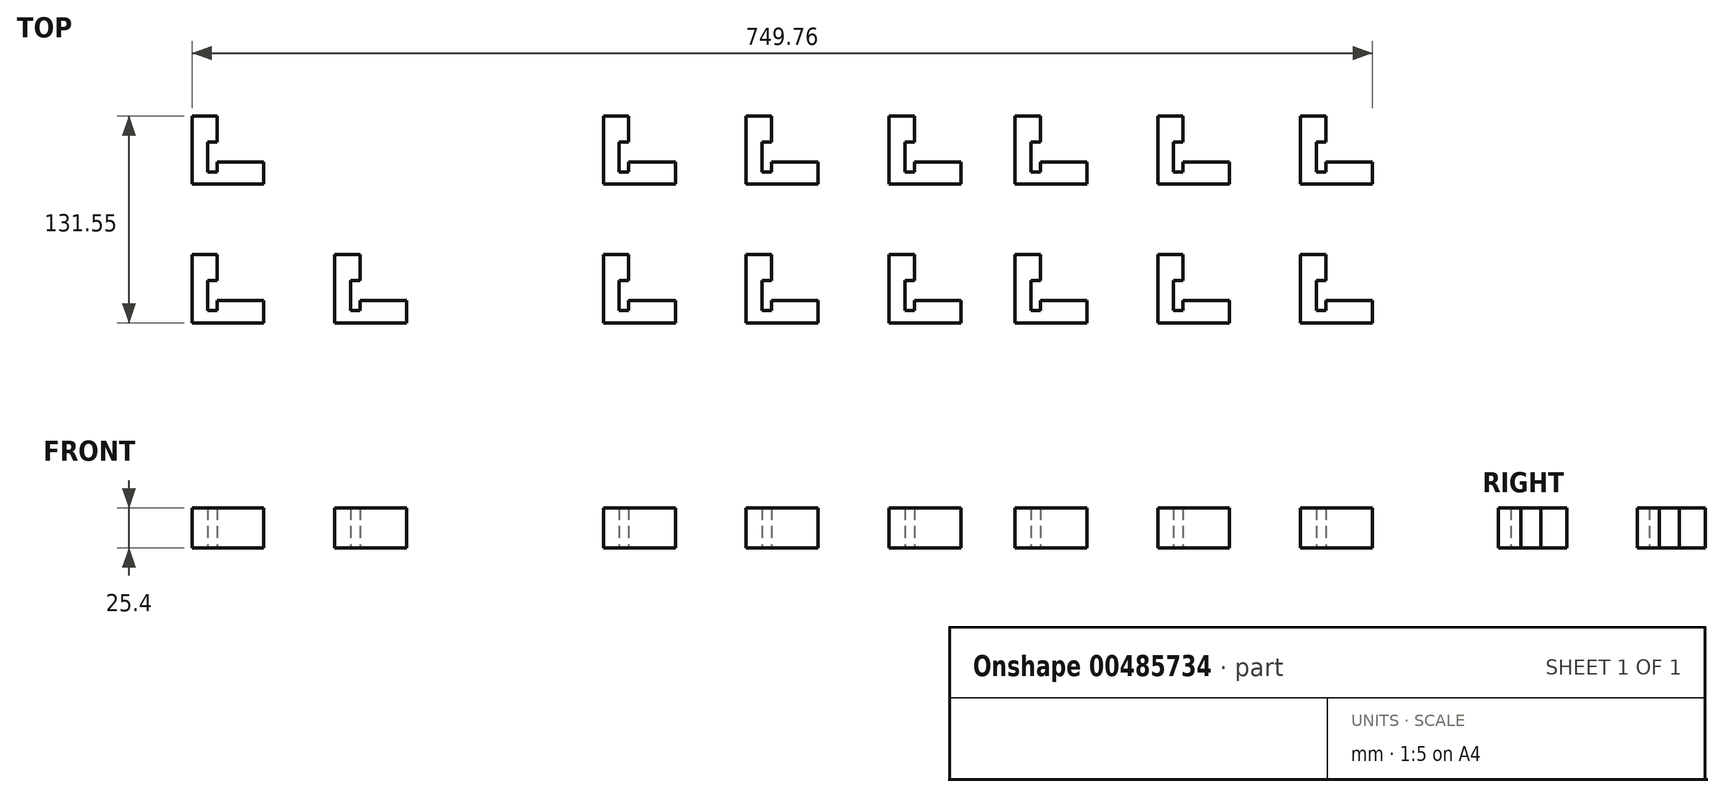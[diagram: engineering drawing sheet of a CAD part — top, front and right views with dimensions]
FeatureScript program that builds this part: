
annotation { "Feature Type Name" : "Feature", "Feature Type Description" : "" }
export const myFeature = defineFeature(function(context is Context, id is Id, definition is map)
    precondition{}
    {
        {
            var Q0;
            Q0=qCreatedBy(makeId("Top.planeOp"),FACE);
            var sketch = newSketch(context, id + "F0", { "sketchPlane" : qUnion([Q0])});
            skLineSegment(sketch, "E0.bottom", {"start": v(-6.8, 62.1) * mm, "end": v(-22.84, 62.1) * mm});
            skLineSegment(sketch, "E0.top", {"start": v(22.84, 18.7) * mm, "end": v(-22.84, 18.7) * mm});
            skLineSegment(sketch, "E0.left", {"start": v(22.84, 32.88) * mm, "end": v(22.84, 18.7) * mm});
            skLineSegment(sketch, "E0.right", {"start": v(-22.84, 62.1) * mm, "end": v(-22.84, 18.7) * mm});
            skLineSegment(sketch, "E1", {"start": v(-6.8, 62.1) * mm, "end": v(-6.8, 45.58) * mm});
            skLineSegment(sketch, "E2", {"start": v(-6.8, 45.58) * mm, "end": v(-12.8, 45.58) * mm});
            skLineSegment(sketch, "E3", {"start": v(-12.8, 45.58) * mm, "end": v(-12.8, 32.88) * mm});
            skLineSegment(sketch, "E4", {"start": v(-6.8, 32.88) * mm, "end": v(22.84, 32.88) * mm});
            skLineSegment(sketch, "E5", {"start": v(-6.8, 32.88) * mm, "end": v(-6.8, 26.57) * mm});
            skLineSegment(sketch, "E6", {"start": v(-6.8, 26.57) * mm, "end": v(-12.8, 26.57) * mm});
            skLineSegment(sketch, "E7", {"start": v(-12.8, 26.57) * mm, "end": v(-12.8, 32.88) * mm});
            skLineSegment(sketch, "E8.0.1.0", {"start": v(-6.8, 150.24) * mm, "end": v(-22.84, 150.24) * mm});
            skLineSegment(sketch, "E8.0.1.1", {"start": v(-6.8, 114.71) * mm, "end": v(-12.8, 114.71) * mm});
            skLineSegment(sketch, "E8.0.1.2", {"start": v(-12.8, 114.71) * mm, "end": v(-12.8, 121.02) * mm});
            skLineSegment(sketch, "E8.0.1.3", {"start": v(-6.8, 121.02) * mm, "end": v(22.84, 121.02) * mm});
            skLineSegment(sketch, "E8.0.1.4", {"start": v(-6.8, 150.24) * mm, "end": v(-6.8, 133.72) * mm});
            skLineSegment(sketch, "E8.0.1.5", {"start": v(-22.84, 150.24) * mm, "end": v(-22.84, 106.83) * mm});
            skLineSegment(sketch, "E8.0.1.6", {"start": v(-6.8, 133.72) * mm, "end": v(-12.8, 133.72) * mm});
            skLineSegment(sketch, "E8.0.1.7", {"start": v(-6.8, 121.02) * mm, "end": v(-6.8, 114.71) * mm});
            skLineSegment(sketch, "E8.0.1.8", {"start": v(-12.8, 133.72) * mm, "end": v(-12.8, 121.02) * mm});
            skLineSegment(sketch, "E8.0.1.9", {"start": v(22.84, 106.83) * mm, "end": v(-22.84, 106.83) * mm});
            skLineSegment(sketch, "E8.0.1.10", {"start": v(22.84, 121.02) * mm, "end": v(22.84, 106.83) * mm});
            skLineSegment(sketch, "E8.1.0.0", {"start": v(83.88, 62.1) * mm, "end": v(67.84, 62.1) * mm});
            skLineSegment(sketch, "E8.1.0.1", {"start": v(83.88, 26.57) * mm, "end": v(77.88, 26.57) * mm});
            skLineSegment(sketch, "E8.1.0.2", {"start": v(77.88, 26.57) * mm, "end": v(77.88, 32.88) * mm});
            skLineSegment(sketch, "E8.1.0.3", {"start": v(83.88, 32.88) * mm, "end": v(113.51, 32.88) * mm});
            skLineSegment(sketch, "E8.1.0.4", {"start": v(83.88, 62.1) * mm, "end": v(83.88, 45.58) * mm});
            skLineSegment(sketch, "E8.1.0.5", {"start": v(67.84, 62.1) * mm, "end": v(67.84, 18.7) * mm});
            skLineSegment(sketch, "E8.1.0.6", {"start": v(83.88, 45.58) * mm, "end": v(77.88, 45.58) * mm});
            skLineSegment(sketch, "E8.1.0.7", {"start": v(83.88, 32.88) * mm, "end": v(83.88, 26.57) * mm});
            skLineSegment(sketch, "E8.1.0.8", {"start": v(77.88, 45.58) * mm, "end": v(77.88, 32.88) * mm});
            skLineSegment(sketch, "E8.1.0.9", {"start": v(113.51, 18.7) * mm, "end": v(67.84, 18.7) * mm});
            skLineSegment(sketch, "E8.1.0.10", {"start": v(113.51, 32.88) * mm, "end": v(113.51, 18.7) * mm});
            skLineSegment(sketch, "E8.1.1.0", {"start": v(83.88, 150.24) * mm, "end": v(67.84, 150.24) * mm});
            skLineSegment(sketch, "E8.1.1.1", {"start": v(83.88, 114.71) * mm, "end": v(77.88, 114.71) * mm});
            skLineSegment(sketch, "E8.1.1.2", {"start": v(77.88, 114.71) * mm, "end": v(77.88, 121.02) * mm});
            skLineSegment(sketch, "E8.1.1.3", {"start": v(83.88, 121.02) * mm, "end": v(113.51, 121.02) * mm});
            skLineSegment(sketch, "E8.1.1.4", {"start": v(83.88, 150.24) * mm, "end": v(83.88, 133.72) * mm});
            skLineSegment(sketch, "E8.1.1.5", {"start": v(67.84, 150.24) * mm, "end": v(67.84, 106.83) * mm});
            skLineSegment(sketch, "E8.1.1.6", {"start": v(83.88, 133.72) * mm, "end": v(77.88, 133.72) * mm});
            skLineSegment(sketch, "E8.1.1.7", {"start": v(83.88, 121.02) * mm, "end": v(83.88, 114.71) * mm});
            skLineSegment(sketch, "E8.1.1.8", {"start": v(77.88, 133.72) * mm, "end": v(77.88, 121.02) * mm});
            skLineSegment(sketch, "E8.1.1.9", {"start": v(113.51, 106.83) * mm, "end": v(67.84, 106.83) * mm});
            skLineSegment(sketch, "E8.1.1.10", {"start": v(113.51, 121.02) * mm, "end": v(113.51, 106.83) * mm});
            skLineSegment(sketch, "E8.2.0.0", {"start": v(174.55, 62.1) * mm, "end": v(158.52, 62.1) * mm});
            skLineSegment(sketch, "E8.2.0.1", {"start": v(174.55, 26.57) * mm, "end": v(168.56, 26.57) * mm});
            skLineSegment(sketch, "E8.2.0.2", {"start": v(168.56, 26.57) * mm, "end": v(168.56, 32.88) * mm});
            skLineSegment(sketch, "E8.2.0.3", {"start": v(174.55, 32.88) * mm, "end": v(204.2, 32.88) * mm});
            skLineSegment(sketch, "E8.2.0.4", {"start": v(174.55, 62.1) * mm, "end": v(174.55, 45.58) * mm});
            skLineSegment(sketch, "E8.2.0.5", {"start": v(158.52, 62.1) * mm, "end": v(158.52, 18.7) * mm});
            skLineSegment(sketch, "E8.2.0.6", {"start": v(174.55, 45.58) * mm, "end": v(168.56, 45.58) * mm});
            skLineSegment(sketch, "E8.2.0.7", {"start": v(174.55, 32.88) * mm, "end": v(174.55, 26.57) * mm});
            skLineSegment(sketch, "E8.2.0.8", {"start": v(168.56, 45.58) * mm, "end": v(168.56, 32.88) * mm});
            skLineSegment(sketch, "E8.2.0.9", {"start": v(204.2, 18.7) * mm, "end": v(158.52, 18.7) * mm});
            skLineSegment(sketch, "E8.2.0.10", {"start": v(204.2, 32.88) * mm, "end": v(204.2, 18.7) * mm});
            skLineSegment(sketch, "E8.2.1.0", {"start": v(174.55, 150.24) * mm, "end": v(158.52, 150.24) * mm});
            skLineSegment(sketch, "E8.2.1.1", {"start": v(174.55, 114.71) * mm, "end": v(168.56, 114.71) * mm});
            skLineSegment(sketch, "E8.2.1.2", {"start": v(168.56, 114.71) * mm, "end": v(168.56, 121.02) * mm});
            skLineSegment(sketch, "E8.2.1.3", {"start": v(174.55, 121.02) * mm, "end": v(204.2, 121.02) * mm});
            skLineSegment(sketch, "E8.2.1.4", {"start": v(174.55, 150.24) * mm, "end": v(174.55, 133.72) * mm});
            skLineSegment(sketch, "E8.2.1.5", {"start": v(158.52, 150.24) * mm, "end": v(158.52, 106.83) * mm});
            skLineSegment(sketch, "E8.2.1.6", {"start": v(174.55, 133.72) * mm, "end": v(168.56, 133.72) * mm});
            skLineSegment(sketch, "E8.2.1.7", {"start": v(174.55, 121.02) * mm, "end": v(174.55, 114.71) * mm});
            skLineSegment(sketch, "E8.2.1.8", {"start": v(168.56, 133.72) * mm, "end": v(168.56, 121.02) * mm});
            skLineSegment(sketch, "E8.2.1.9", {"start": v(204.2, 106.83) * mm, "end": v(158.52, 106.83) * mm});
            skLineSegment(sketch, "E8.2.1.10", {"start": v(204.2, 121.02) * mm, "end": v(204.2, 106.83) * mm});
            skLineSegment(sketch, "E9.1.0.0", {"start": v(435.92, 121.02) * mm, "end": v(465.56, 121.02) * mm});
            skLineSegment(sketch, "E9.1.0.1", {"start": v(254.56, 32.88) * mm, "end": v(284.2, 32.88) * mm});
            skLineSegment(sketch, "E9.1.0.2", {"start": v(345.24, 32.88) * mm, "end": v(374.88, 32.88) * mm});
            skLineSegment(sketch, "E9.1.0.3", {"start": v(419.89, 150.24) * mm, "end": v(419.89, 106.83) * mm});
            skLineSegment(sketch, "E9.1.0.4", {"start": v(254.56, 62.1) * mm, "end": v(254.56, 45.58) * mm});
            skLineSegment(sketch, "E9.1.0.5", {"start": v(284.2, 121.02) * mm, "end": v(284.2, 106.83) * mm});
            skLineSegment(sketch, "E9.1.0.6", {"start": v(374.88, 32.88) * mm, "end": v(374.88, 18.7) * mm});
            skLineSegment(sketch, "E9.1.0.7", {"start": v(465.56, 32.88) * mm, "end": v(465.56, 18.7) * mm});
            skLineSegment(sketch, "E9.1.0.8", {"start": v(284.2, 32.88) * mm, "end": v(284.2, 18.7) * mm});
            skLineSegment(sketch, "E9.1.0.9", {"start": v(329.2, 62.1) * mm, "end": v(329.2, 18.7) * mm});
            skLineSegment(sketch, "E9.1.0.10", {"start": v(329.2, 150.24) * mm, "end": v(329.2, 106.83) * mm});
            skLineSegment(sketch, "E9.1.0.11", {"start": v(254.56, 62.1) * mm, "end": v(238.53, 62.1) * mm});
            skLineSegment(sketch, "E9.1.0.12", {"start": v(435.92, 62.1) * mm, "end": v(419.89, 62.1) * mm});
            skLineSegment(sketch, "E9.1.0.13", {"start": v(465.56, 121.02) * mm, "end": v(465.56, 106.83) * mm});
            skLineSegment(sketch, "E9.1.0.14", {"start": v(345.24, 62.1) * mm, "end": v(329.2, 62.1) * mm});
            skLineSegment(sketch, "E9.1.0.15", {"start": v(374.88, 18.7) * mm, "end": v(329.2, 18.7) * mm});
            skLineSegment(sketch, "E9.1.0.16", {"start": v(254.56, 150.24) * mm, "end": v(254.56, 133.72) * mm});
            skLineSegment(sketch, "E9.1.0.17", {"start": v(284.2, 18.7) * mm, "end": v(238.53, 18.7) * mm});
            skLineSegment(sketch, "E9.1.0.18", {"start": v(435.92, 150.24) * mm, "end": v(419.89, 150.24) * mm});
            skLineSegment(sketch, "E9.1.0.19", {"start": v(339.25, 45.58) * mm, "end": v(339.25, 32.88) * mm});
            skLineSegment(sketch, "E9.1.0.20", {"start": v(435.92, 32.88) * mm, "end": v(465.56, 32.88) * mm});
            skLineSegment(sketch, "E9.1.0.21", {"start": v(435.92, 62.1) * mm, "end": v(435.92, 45.58) * mm});
            skLineSegment(sketch, "E9.1.0.22", {"start": v(345.24, 150.24) * mm, "end": v(329.2, 150.24) * mm});
            skLineSegment(sketch, "E9.1.0.23", {"start": v(345.24, 62.1) * mm, "end": v(345.24, 45.58) * mm});
            skLineSegment(sketch, "E9.1.0.24", {"start": v(254.56, 121.02) * mm, "end": v(284.2, 121.02) * mm});
            skLineSegment(sketch, "E9.1.0.25", {"start": v(284.2, 106.83) * mm, "end": v(238.53, 106.83) * mm});
            skLineSegment(sketch, "E9.1.0.26", {"start": v(345.24, 121.02) * mm, "end": v(374.88, 121.02) * mm});
            skLineSegment(sketch, "E9.1.0.27", {"start": v(465.56, 18.7) * mm, "end": v(419.89, 18.7) * mm});
            skLineSegment(sketch, "E9.1.0.28", {"start": v(419.89, 62.1) * mm, "end": v(419.89, 18.7) * mm});
            skLineSegment(sketch, "E9.1.0.29", {"start": v(465.56, 106.83) * mm, "end": v(419.89, 106.83) * mm});
            skLineSegment(sketch, "E9.1.0.30", {"start": v(374.88, 106.83) * mm, "end": v(329.2, 106.83) * mm});
            skLineSegment(sketch, "E9.1.0.31", {"start": v(238.53, 62.1) * mm, "end": v(238.53, 18.7) * mm});
            skLineSegment(sketch, "E9.1.0.32", {"start": v(254.56, 150.24) * mm, "end": v(238.53, 150.24) * mm});
            skLineSegment(sketch, "E9.1.0.33", {"start": v(238.53, 150.24) * mm, "end": v(238.53, 106.83) * mm});
            skLineSegment(sketch, "E9.1.0.34", {"start": v(435.92, 150.24) * mm, "end": v(435.92, 133.72) * mm});
            skLineSegment(sketch, "E9.1.0.35", {"start": v(429.93, 133.72) * mm, "end": v(429.93, 121.02) * mm});
            skLineSegment(sketch, "E9.1.0.36", {"start": v(345.24, 150.24) * mm, "end": v(345.24, 133.72) * mm});
            skLineSegment(sketch, "E9.1.0.37", {"start": v(374.88, 121.02) * mm, "end": v(374.88, 106.83) * mm});
            skLineSegment(sketch, "E9.1.0.38", {"start": v(429.93, 45.58) * mm, "end": v(429.93, 32.88) * mm});
            skLineSegment(sketch, "E9.1.0.39", {"start": v(345.24, 121.02) * mm, "end": v(345.24, 114.71) * mm});
            skLineSegment(sketch, "E9.1.0.40", {"start": v(339.25, 114.71) * mm, "end": v(339.25, 121.02) * mm});
            skLineSegment(sketch, "E9.1.0.41", {"start": v(345.24, 133.72) * mm, "end": v(339.25, 133.72) * mm});
            skLineSegment(sketch, "E9.1.0.42", {"start": v(339.25, 26.57) * mm, "end": v(339.25, 32.88) * mm});
            skLineSegment(sketch, "E9.1.0.43", {"start": v(248.57, 26.57) * mm, "end": v(248.57, 32.88) * mm});
            skLineSegment(sketch, "E9.1.0.44", {"start": v(254.56, 32.88) * mm, "end": v(254.56, 26.57) * mm});
            skLineSegment(sketch, "E9.1.0.45", {"start": v(248.57, 114.71) * mm, "end": v(248.57, 121.02) * mm});
            skLineSegment(sketch, "E9.1.0.46", {"start": v(429.93, 26.57) * mm, "end": v(429.93, 32.88) * mm});
            skLineSegment(sketch, "E9.1.0.47", {"start": v(248.57, 45.58) * mm, "end": v(248.57, 32.88) * mm});
            skLineSegment(sketch, "E9.1.0.48", {"start": v(345.24, 45.58) * mm, "end": v(339.25, 45.58) * mm});
            skLineSegment(sketch, "E9.1.0.49", {"start": v(345.24, 26.57) * mm, "end": v(339.25, 26.57) * mm});
            skLineSegment(sketch, "E9.1.0.50", {"start": v(254.56, 121.02) * mm, "end": v(254.56, 114.71) * mm});
            skLineSegment(sketch, "E9.1.0.51", {"start": v(435.92, 32.88) * mm, "end": v(435.92, 26.57) * mm});
            skLineSegment(sketch, "E9.1.0.52", {"start": v(435.92, 26.57) * mm, "end": v(429.93, 26.57) * mm});
            skLineSegment(sketch, "E9.1.0.53", {"start": v(248.57, 133.72) * mm, "end": v(248.57, 121.02) * mm});
            skLineSegment(sketch, "E9.1.0.54", {"start": v(254.56, 26.57) * mm, "end": v(248.57, 26.57) * mm});
            skLineSegment(sketch, "E9.1.0.55", {"start": v(435.92, 121.02) * mm, "end": v(435.92, 114.71) * mm});
            skLineSegment(sketch, "E9.1.0.56", {"start": v(345.24, 32.88) * mm, "end": v(345.24, 26.57) * mm});
            skLineSegment(sketch, "E9.1.0.57", {"start": v(435.92, 133.72) * mm, "end": v(429.93, 133.72) * mm});
            skLineSegment(sketch, "E9.1.0.58", {"start": v(339.25, 133.72) * mm, "end": v(339.25, 121.02) * mm});
            skLineSegment(sketch, "E9.1.0.59", {"start": v(254.56, 133.72) * mm, "end": v(248.57, 133.72) * mm});
            skLineSegment(sketch, "E9.1.0.60", {"start": v(345.24, 114.71) * mm, "end": v(339.25, 114.71) * mm});
            skLineSegment(sketch, "E9.1.0.61", {"start": v(435.92, 45.58) * mm, "end": v(429.93, 45.58) * mm});
            skLineSegment(sketch, "E9.1.0.62", {"start": v(435.92, 114.71) * mm, "end": v(429.93, 114.71) * mm});
            skLineSegment(sketch, "E9.1.0.63", {"start": v(254.56, 114.71) * mm, "end": v(248.57, 114.71) * mm});
            skLineSegment(sketch, "E9.1.0.64", {"start": v(429.93, 114.71) * mm, "end": v(429.93, 121.02) * mm});
            skLineSegment(sketch, "E9.1.0.65", {"start": v(254.56, 45.58) * mm, "end": v(248.57, 45.58) * mm});
            skLineSegment(sketch, "E9.2.0.0", {"start": v(697.29, 121.02) * mm, "end": v(726.92, 121.02) * mm});
            skLineSegment(sketch, "E9.2.0.1", {"start": v(515.93, 32.88) * mm, "end": v(545.57, 32.88) * mm});
            skLineSegment(sketch, "E9.2.0.2", {"start": v(606.6, 32.88) * mm, "end": v(636.25, 32.88) * mm});
            skLineSegment(sketch, "E9.2.0.3", {"start": v(681.25, 150.24) * mm, "end": v(681.25, 106.83) * mm});
            skLineSegment(sketch, "E9.2.0.4", {"start": v(515.93, 62.1) * mm, "end": v(515.93, 45.58) * mm});
            skLineSegment(sketch, "E9.2.0.5", {"start": v(545.57, 121.02) * mm, "end": v(545.57, 106.83) * mm});
            skLineSegment(sketch, "E9.2.0.6", {"start": v(636.25, 32.88) * mm, "end": v(636.25, 18.7) * mm});
            skLineSegment(sketch, "E9.2.0.7", {"start": v(726.92, 32.88) * mm, "end": v(726.92, 18.7) * mm});
            skLineSegment(sketch, "E9.2.0.8", {"start": v(545.57, 32.88) * mm, "end": v(545.57, 18.7) * mm});
            skLineSegment(sketch, "E9.2.0.9", {"start": v(590.57, 62.1) * mm, "end": v(590.57, 18.7) * mm});
            skLineSegment(sketch, "E9.2.0.10", {"start": v(590.57, 150.24) * mm, "end": v(590.57, 106.83) * mm});
            skLineSegment(sketch, "E9.2.0.11", {"start": v(515.93, 62.1) * mm, "end": v(499.9, 62.1) * mm});
            skLineSegment(sketch, "E9.2.0.12", {"start": v(697.29, 62.1) * mm, "end": v(681.25, 62.1) * mm});
            skLineSegment(sketch, "E9.2.0.13", {"start": v(726.92, 121.02) * mm, "end": v(726.92, 106.83) * mm});
            skLineSegment(sketch, "E9.2.0.14", {"start": v(606.6, 62.1) * mm, "end": v(590.57, 62.1) * mm});
            skLineSegment(sketch, "E9.2.0.15", {"start": v(636.25, 18.7) * mm, "end": v(590.57, 18.7) * mm});
            skLineSegment(sketch, "E9.2.0.16", {"start": v(515.93, 150.24) * mm, "end": v(515.93, 133.72) * mm});
            skLineSegment(sketch, "E9.2.0.17", {"start": v(545.57, 18.7) * mm, "end": v(499.9, 18.7) * mm});
            skLineSegment(sketch, "E9.2.0.18", {"start": v(697.29, 150.24) * mm, "end": v(681.25, 150.24) * mm});
            skLineSegment(sketch, "E9.2.0.19", {"start": v(600.61, 45.58) * mm, "end": v(600.61, 32.88) * mm});
            skLineSegment(sketch, "E9.2.0.20", {"start": v(697.29, 32.88) * mm, "end": v(726.92, 32.88) * mm});
            skLineSegment(sketch, "E9.2.0.21", {"start": v(697.29, 62.1) * mm, "end": v(697.29, 45.58) * mm});
            skLineSegment(sketch, "E9.2.0.22", {"start": v(606.6, 150.24) * mm, "end": v(590.57, 150.24) * mm});
            skLineSegment(sketch, "E9.2.0.23", {"start": v(606.6, 62.1) * mm, "end": v(606.6, 45.58) * mm});
            skLineSegment(sketch, "E9.2.0.24", {"start": v(515.93, 121.02) * mm, "end": v(545.57, 121.02) * mm});
            skLineSegment(sketch, "E9.2.0.25", {"start": v(545.57, 106.83) * mm, "end": v(499.9, 106.83) * mm});
            skLineSegment(sketch, "E9.2.0.26", {"start": v(606.6, 121.02) * mm, "end": v(636.25, 121.02) * mm});
            skLineSegment(sketch, "E9.2.0.27", {"start": v(726.92, 18.7) * mm, "end": v(681.25, 18.7) * mm});
            skLineSegment(sketch, "E9.2.0.28", {"start": v(681.25, 62.1) * mm, "end": v(681.25, 18.7) * mm});
            skLineSegment(sketch, "E9.2.0.29", {"start": v(726.92, 106.83) * mm, "end": v(681.25, 106.83) * mm});
            skLineSegment(sketch, "E9.2.0.30", {"start": v(636.25, 106.83) * mm, "end": v(590.57, 106.83) * mm});
            skLineSegment(sketch, "E9.2.0.31", {"start": v(499.9, 62.1) * mm, "end": v(499.9, 18.7) * mm});
            skLineSegment(sketch, "E9.2.0.32", {"start": v(515.93, 150.24) * mm, "end": v(499.9, 150.24) * mm});
            skLineSegment(sketch, "E9.2.0.33", {"start": v(499.9, 150.24) * mm, "end": v(499.9, 106.83) * mm});
            skLineSegment(sketch, "E9.2.0.34", {"start": v(697.29, 150.24) * mm, "end": v(697.29, 133.72) * mm});
            skLineSegment(sketch, "E9.2.0.35", {"start": v(691.3, 133.72) * mm, "end": v(691.3, 121.02) * mm});
            skLineSegment(sketch, "E9.2.0.36", {"start": v(606.6, 150.24) * mm, "end": v(606.6, 133.72) * mm});
            skLineSegment(sketch, "E9.2.0.37", {"start": v(636.25, 121.02) * mm, "end": v(636.25, 106.83) * mm});
            skLineSegment(sketch, "E9.2.0.38", {"start": v(691.3, 45.58) * mm, "end": v(691.3, 32.88) * mm});
            skLineSegment(sketch, "E9.2.0.39", {"start": v(606.6, 121.02) * mm, "end": v(606.6, 114.71) * mm});
            skLineSegment(sketch, "E9.2.0.40", {"start": v(600.61, 114.71) * mm, "end": v(600.61, 121.02) * mm});
            skLineSegment(sketch, "E9.2.0.41", {"start": v(606.6, 133.72) * mm, "end": v(600.61, 133.72) * mm});
            skLineSegment(sketch, "E9.2.0.42", {"start": v(600.61, 26.57) * mm, "end": v(600.61, 32.88) * mm});
            skLineSegment(sketch, "E9.2.0.43", {"start": v(509.94, 26.57) * mm, "end": v(509.94, 32.88) * mm});
            skLineSegment(sketch, "E9.2.0.44", {"start": v(515.93, 32.88) * mm, "end": v(515.93, 26.57) * mm});
            skLineSegment(sketch, "E9.2.0.45", {"start": v(509.94, 114.71) * mm, "end": v(509.94, 121.02) * mm});
            skLineSegment(sketch, "E9.2.0.46", {"start": v(691.3, 26.57) * mm, "end": v(691.3, 32.88) * mm});
            skLineSegment(sketch, "E9.2.0.47", {"start": v(509.94, 45.58) * mm, "end": v(509.94, 32.88) * mm});
            skLineSegment(sketch, "E9.2.0.48", {"start": v(606.6, 45.58) * mm, "end": v(600.61, 45.58) * mm});
            skLineSegment(sketch, "E9.2.0.49", {"start": v(606.6, 26.57) * mm, "end": v(600.61, 26.57) * mm});
            skLineSegment(sketch, "E9.2.0.50", {"start": v(515.93, 121.02) * mm, "end": v(515.93, 114.71) * mm});
            skLineSegment(sketch, "E9.2.0.51", {"start": v(697.29, 32.88) * mm, "end": v(697.29, 26.57) * mm});
            skLineSegment(sketch, "E9.2.0.52", {"start": v(697.29, 26.57) * mm, "end": v(691.3, 26.57) * mm});
            skLineSegment(sketch, "E9.2.0.53", {"start": v(509.94, 133.72) * mm, "end": v(509.94, 121.02) * mm});
            skLineSegment(sketch, "E9.2.0.54", {"start": v(515.93, 26.57) * mm, "end": v(509.94, 26.57) * mm});
            skLineSegment(sketch, "E9.2.0.55", {"start": v(697.29, 121.02) * mm, "end": v(697.29, 114.71) * mm});
            skLineSegment(sketch, "E9.2.0.56", {"start": v(606.6, 32.88) * mm, "end": v(606.6, 26.57) * mm});
            skLineSegment(sketch, "E9.2.0.57", {"start": v(697.29, 133.72) * mm, "end": v(691.3, 133.72) * mm});
            skLineSegment(sketch, "E9.2.0.58", {"start": v(600.61, 133.72) * mm, "end": v(600.61, 121.02) * mm});
            skLineSegment(sketch, "E9.2.0.59", {"start": v(515.93, 133.72) * mm, "end": v(509.94, 133.72) * mm});
            skLineSegment(sketch, "E9.2.0.60", {"start": v(606.6, 114.71) * mm, "end": v(600.61, 114.71) * mm});
            skLineSegment(sketch, "E9.2.0.61", {"start": v(697.29, 45.58) * mm, "end": v(691.3, 45.58) * mm});
            skLineSegment(sketch, "E9.2.0.62", {"start": v(697.29, 114.71) * mm, "end": v(691.3, 114.71) * mm});
            skLineSegment(sketch, "E9.2.0.63", {"start": v(515.93, 114.71) * mm, "end": v(509.94, 114.71) * mm});
            skLineSegment(sketch, "E9.2.0.64", {"start": v(691.3, 114.71) * mm, "end": v(691.3, 121.02) * mm});
            skLineSegment(sketch, "E9.2.0.65", {"start": v(515.93, 45.58) * mm, "end": v(509.94, 45.58) * mm});
            skLineSegment(sketch, "E9.direction1", {"start": v(-22.84, 18.7) * mm, "end": v(238.53, 18.7) * mm, "construction": true});
            skSolve(sketch);
        }
        {
            var Q0;
            Q0 = qSketchRegion(id + "F0", true);
            extrude(context, id + "F1", {"entities" : qUnion([Q0]), "depth" : 25.4 * mm});
        }
        {
            var Q0;
            Q0=makeQuery(id+"F1.opExtrude","SWEPT_BODY",BODY,{"disambiguationData":[OSD([sQuery(id+"F0.wireOp",EDGE,"E8.2.1.0"),sQuery(id+"F0.wireOp",EDGE,"E8.2.1.1"),sQuery(id+"F0.wireOp",EDGE,"E8.2.1.2"),sQuery(id+"F0.wireOp",EDGE,"E8.2.1.3"),sQuery(id+"F0.wireOp",EDGE,"E8.2.1.4"),sQuery(id+"F0.wireOp",EDGE,"E8.2.1.5"),sQuery(id+"F0.wireOp",EDGE,"E8.2.1.6"),sQuery(id+"F0.wireOp",EDGE,"E8.2.1.7"),sQuery(id+"F0.wireOp",EDGE,"E8.2.1.8"),sQuery(id+"F0.wireOp",EDGE,"E8.2.1.9"),sQuery(id+"F0.wireOp",EDGE,"E8.2.1.10")])]});
            deleteBodies(context, id + "F2", {"entities" : qUnion([Q0])});
        }
        {
            var Q0;
            Q0=makeQuery(id+"F1.opExtrude","SWEPT_BODY",BODY,{"disambiguationData":[OSD([sQuery(id+"F0.wireOp",EDGE,"E8.2.0.0"),sQuery(id+"F0.wireOp",EDGE,"E8.2.0.1"),sQuery(id+"F0.wireOp",EDGE,"E8.2.0.2"),sQuery(id+"F0.wireOp",EDGE,"E8.2.0.3"),sQuery(id+"F0.wireOp",EDGE,"E8.2.0.4"),sQuery(id+"F0.wireOp",EDGE,"E8.2.0.5"),sQuery(id+"F0.wireOp",EDGE,"E8.2.0.6"),sQuery(id+"F0.wireOp",EDGE,"E8.2.0.7"),sQuery(id+"F0.wireOp",EDGE,"E8.2.0.8"),sQuery(id+"F0.wireOp",EDGE,"E8.2.0.9"),sQuery(id+"F0.wireOp",EDGE,"E8.2.0.10")])]});
            deleteBodies(context, id + "F3", {"entities" : qUnion([Q0])});
        }
        {
            var Q0;
            Q0=makeQuery(id+"F1.opExtrude","SWEPT_BODY",BODY,{"disambiguationData":[OSD([sQuery(id+"F0.wireOp",EDGE,"E8.1.1.0"),sQuery(id+"F0.wireOp",EDGE,"E8.1.1.1"),sQuery(id+"F0.wireOp",EDGE,"E8.1.1.2"),sQuery(id+"F0.wireOp",EDGE,"E8.1.1.3"),sQuery(id+"F0.wireOp",EDGE,"E8.1.1.4"),sQuery(id+"F0.wireOp",EDGE,"E8.1.1.5"),sQuery(id+"F0.wireOp",EDGE,"E8.1.1.6"),sQuery(id+"F0.wireOp",EDGE,"E8.1.1.7"),sQuery(id+"F0.wireOp",EDGE,"E8.1.1.8"),sQuery(id+"F0.wireOp",EDGE,"E8.1.1.9"),sQuery(id+"F0.wireOp",EDGE,"E8.1.1.10")])]});
            deleteBodies(context, id + "F4", {"entities" : qUnion([Q0])});
        }
    });
